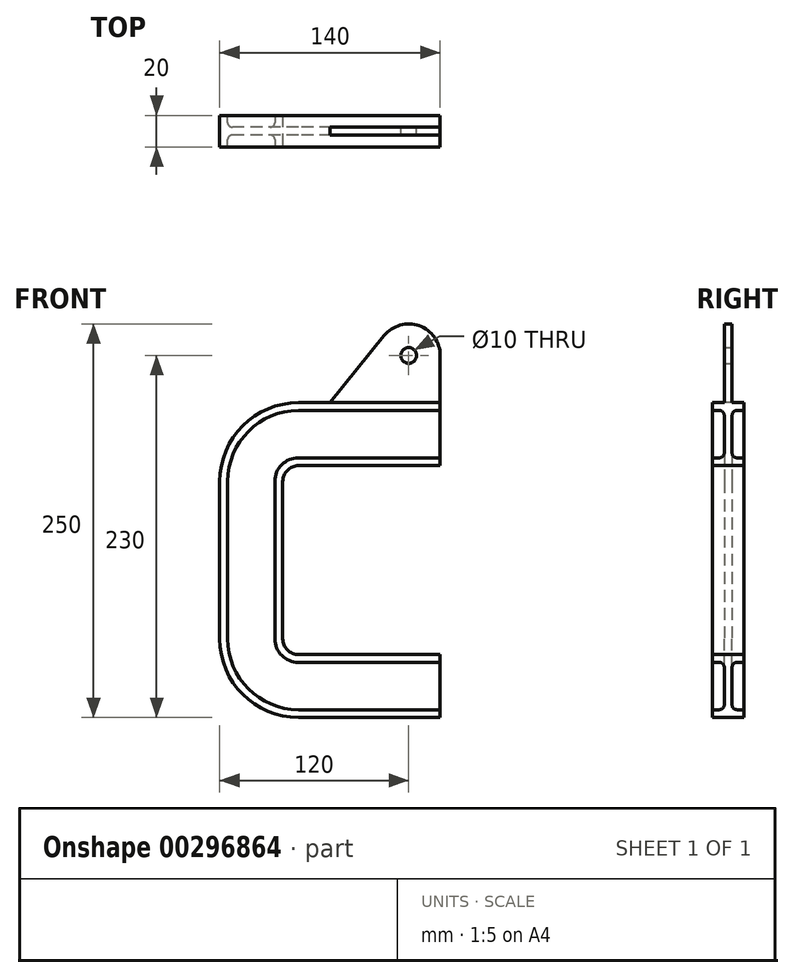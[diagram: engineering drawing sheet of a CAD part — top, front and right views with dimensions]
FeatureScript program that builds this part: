
annotation { "Feature Type Name" : "Feature", "Feature Type Description" : "" }
export const myFeature = defineFeature(function(context is Context, id is Id, definition is map)
    precondition{}
    {
        {
            var Q0;
            Q0=qCreatedBy(makeId("Front.planeOp"),FACE);
            var sketch = newSketch(context, id + "F0", { "sketchPlane" : qUnion([Q0])});
            skLineSegment(sketch, "E0", {"start": v(0, 60) * mm, "end": v(-90, 60) * mm});
            skArc(sketch, "E1", {"start": v(-90, 60) * mm, "mid": v(-97.07, 57.07) * mm, "end": v(-100, 50) * mm});
            skLineSegment(sketch, "E2", {"start": v(-100, 50) * mm, "end": v(-100, 0) * mm});
            skSolve(sketch);
        }
        {
            var Q0;
            Q0=qCreatedBy(makeId("Right.planeOp"),FACE);
            var sketch = newSketch(context, id + "F1", { "sketchPlane" : qUnion([Q0])});
            skLineSegment(sketch, "E3", {"start": v(10, 100) * mm, "end": v(-10, 100) * mm});
            skLineSegment(sketch, "E4", {"start": v(-10, 100) * mm, "end": v(-10, 95) * mm});
            skLineSegment(sketch, "E5", {"start": v(-10, 95) * mm, "end": v(-5.5, 95) * mm});
            skLineSegment(sketch, "E6", {"start": v(-2.5, 92) * mm, "end": v(-2.5, 68) * mm});
            skLineSegment(sketch, "E7", {"start": v(-5.5, 65) * mm, "end": v(-10, 65) * mm});
            skLineSegment(sketch, "E8", {"start": v(-10, 65) * mm, "end": v(-10, 60) * mm});
            skLineSegment(sketch, "E9", {"start": v(10, 60) * mm, "end": v(10, 65) * mm});
            skLineSegment(sketch, "E10", {"start": v(10, 65) * mm, "end": v(5.5, 65) * mm});
            skLineSegment(sketch, "E11", {"start": v(2.5, 68) * mm, "end": v(2.5, 92) * mm});
            skLineSegment(sketch, "E12", {"start": v(5.5, 95) * mm, "end": v(10, 95) * mm});
            skLineSegment(sketch, "E13", {"start": v(10, 95) * mm, "end": v(10, 100) * mm});
            skLineSegment(sketch, "E14", {"start": v(10, 60) * mm, "end": v(0, 60) * mm});
            skLineSegment(sketch, "E15", {"start": v(0, 60) * mm, "end": v(-10, 60) * mm});
            skPoint(sketch, "E16.visualSharp", {"position": v(2.5, 95) * mm});
            skArc(sketch, "E16.filletArc", {"start": v(5.5, 95) * mm, "mid": v(3.38, 94.12) * mm, "end": v(2.5, 92) * mm});
            skPoint(sketch, "E17.visualSharp", {"position": v(-2.5, 95) * mm});
            skArc(sketch, "E17.filletArc", {"start": v(-2.5, 92) * mm, "mid": v(-3.38, 94.12) * mm, "end": v(-5.5, 95) * mm});
            skPoint(sketch, "E18.visualSharp", {"position": v(2.5, 65) * mm});
            skArc(sketch, "E18.filletArc", {"start": v(2.5, 68) * mm, "mid": v(3.38, 65.88) * mm, "end": v(5.5, 65) * mm});
            skPoint(sketch, "E19.visualSharp", {"position": v(-2.5, 65) * mm});
            skArc(sketch, "E19.filletArc", {"start": v(-5.5, 65) * mm, "mid": v(-3.38, 65.88) * mm, "end": v(-2.5, 68) * mm});
            skSolve(sketch);
        }
        {
            var Q0;
            Q0=makeQuery(id+"F1.imprint","IMPRINT",FACE,{"disambiguationData":[TD([[makeQuery(id+"F1.imprint","IMPRINT",EDGE,{"derivedFrom":sQuery(id+"F1.wireOp",EDGE,"E3")}),1.0]])]});
            var Q1;
            Q1=sQuery(id+"F0.wireOp",EDGE,"E0");
            var Q2;
            Q2=sQuery(id+"F0.wireOp",EDGE,"E1");
            var Q3;
            Q3=sQuery(id+"F0.wireOp",EDGE,"E2");
            sweep(context, id + "F2", {"profiles" : qUnion([Q0]), "path" : qUnion([Q1, Q2, Q3])});
        }
        {
            var Q0;
            Q0=makeQuery(id+"F2.opSweep","SWEPT_BODY",BODY,{"disambiguationData":[OSD([sQuery(id+"F0.wireOp",EDGE,"E2"),sQuery(id+"F1.wireOp",EDGE,"E3"),sQuery(id+"F1.wireOp",EDGE,"E4"),sQuery(id+"F1.wireOp",EDGE,"E5"),sQuery(id+"F1.wireOp",EDGE,"E6"),sQuery(id+"F1.wireOp",EDGE,"E7"),sQuery(id+"F1.wireOp",EDGE,"E8"),sQuery(id+"F1.wireOp",EDGE,"E9"),sQuery(id+"F1.wireOp",EDGE,"E10"),sQuery(id+"F1.wireOp",EDGE,"E11"),sQuery(id+"F1.wireOp",EDGE,"E12"),sQuery(id+"F1.wireOp",EDGE,"E13"),sQuery(id+"F1.wireOp",EDGE,"E14"),sQuery(id+"F1.wireOp",EDGE,"E15"),sQuery(id+"F1.wireOp",EDGE,"E16.filletArc"),sQuery(id+"F1.wireOp",EDGE,"E17.filletArc"),sQuery(id+"F1.wireOp",EDGE,"E18.filletArc"),sQuery(id+"F1.wireOp",EDGE,"E19.filletArc")])]});
            var Q1;
            Q1=qCreatedBy(makeId("Top.planeOp"),FACE);
            mirror(context, id + "F3", {"operationType" : NewBodyOperationType.ADD, "entities" : qUnion([Q0]), "mirrorPlane" : qUnion([Q1])});
        }
        {
            var Q0;
            Q0=qCreatedBy(makeId("Front.planeOp"),FACE);
            var sketch = newSketch(context, id + "F4", { "sketchPlane" : qUnion([Q0])});
            skLineSegment(sketch, "E20", {"start": v(0, 130) * mm, "end": v(0, 100) * mm});
            skLineSegment(sketch, "E21", {"start": v(0, 100) * mm, "end": v(-70, 100) * mm});
            skLineSegment(sketch, "E22", {"start": v(-70, 100) * mm, "end": v(-35.55, 142.58) * mm});
            skPoint(sketch, "E23.visualSharp", {"position": v(80.8, 77.95) * mm});
            skArc(sketch, "E23.filletArc", {"start": v(0, 130) * mm, "mid": v(-13.33, 148.85) * mm, "end": v(-35.55, 142.58) * mm});
            skCircle(sketch, "E24", {"center": v(-20, 130) * mm, "radius": 5 * mm});
            skLineSegment(sketch, "E25.MirrorCS", {"start": v(-70, -100) * mm, "end": v(-35.55, -142.58) * mm});
            skLineSegment(sketch, "E26.MirrorCS", {"start": v(0, -100) * mm, "end": v(-70, -100) * mm});
            skLineSegment(sketch, "E27.MirrorCS", {"start": v(0, -130) * mm, "end": v(0, -100) * mm});
            skArc(sketch, "E28.MirrorCS", {"start": v(0, -130) * mm, "mid": v(-13.33, -148.85) * mm, "end": v(-35.55, -142.58) * mm});
            skCircle(sketch, "E29.MirrorC", {"center": v(-20, -130) * mm, "radius": 5 * mm});
            skSolve(sketch);
        }
        {
            var Q0;
            Q0=makeQuery(id+"F4.imprint","IMPRINT",FACE,{"disambiguationData":[TD([[makeQuery(id+"F4.imprint","IMPRINT",EDGE,{"derivedFrom":sQuery(id+"F4.wireOp",EDGE,"E20")}),-1.0]])]});
            var Q1;
            Q1=makeQuery(id+"F4.imprint","IMPRINT",FACE,{"disambiguationData":[TD([[makeQuery(id+"F4.imprint","IMPRINT",EDGE,{"derivedFrom":sQuery(id+"F4.wireOp",EDGE,"E28.MirrorCS")}),-1.0]])]});
            extrude(context, id + "F5", {"entities" : qUnion([Q0, Q1]), "operationType" : NewBodyOperationType.ADD, "endBound" : BoundingType.SYMMETRIC, "depth" : 5 * mm});
        }
    });
